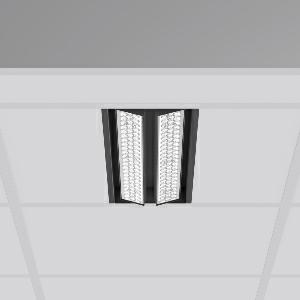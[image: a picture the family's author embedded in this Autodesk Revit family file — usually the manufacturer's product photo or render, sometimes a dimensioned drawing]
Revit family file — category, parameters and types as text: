
# Revit family: tx-move_901738_003_76_d800
name_source: partatom
category: Lighting Fixtures
units: mm (PartAtom-declared; Revit-internal decimal feet)

## family parameters
Cut with Voids When Loaded = No
Host = Face
Light Source = No
Part Type = Normal
Room Calculation Point = No
Round Connector Dimension = Use Diameter
Shared = No

## types (1)
- MultiLumen 1 (1 x LED Modul 830, 2625 lm, 3000)
    Apparent Load = 35 VA
    Approval mark = CE
    CIE Flux Codes = 65 90 98 100 100
    Color Rendering = 80
    Color Temperature = 3000
    Default Elevation = 1800 mm
    Description = Series: TX-MOVE
Einlege/Einbau-Flächenstrahler. Housing: sheet steel, powder-coated. 2xSwivel range: 90°. High-efficiency LED units with optimum light control thanks to clear plastic (PC) lens optics. Spezielle Mikrostrukturen reduzieren Gelbsaum. Asymmetrical light distribution. Suitable for laying in grid ceiling module 625. Connected converter included in separate gearbox.Suitable for through-wiring.MultiLumen: Luminous flux adjustable in 3 steps. Accessories: Mounting frame for installation in suspended ceilings. Environmentally friendly and resource-saving due to replaceable and recyclable components. 
Colour: deep black, matt (RAL 9005)
Length: 622 mm
Width: 190 mm
Height: 39 mm
Cut-out length: 602 mm
Cut-out width: 174 mm
Recess height: 100 mm
Lamp: LED
Socket: without socket
Colour temperature: 3000K
Colour rendering index (CRI): 80
System power: 35 W
Rated luminous flux: 5250 lm
Luminous efficiency: 150 lm/W
System power 2: 47 W
Rated luminous flux 2: 6800 lm
Luminous efficiency 2: 145 lm/W
System power 3: 68 W
Rated luminous flux 3: 9250 lm
Luminous efficiency 3: 136 lm/W
Control gear: Dimmable EVG, DALI
Protection class: I
Type of protection: IP 20
    Height = 0 mm  [stored 0 ft]
    Lamp = 1 x LED Modul 830
    Lamp Light Flux = 2625 lm
    Lamp count = 1
    Length = 622 mm
    Lifetime = 50000 h
    Luminous efficacy = 150 lm/W
    Manufacturer = RZB
    ModVariant = No
    Model = 901738.003.76
    Mounting Place = Ceiling, Wall
    Mounting Type = Recessed
    Number of Poles = 1
    OnlyDefault = Yes
    Power Factor = 1
    Product Name = TX-MOVE
    Product group = Recessed projectors
    ProductGroupID = 401
    Protection Class = Protection class I
    Protection Degree = IP 20
    RLX_Detail_Level = 1
    RLX_Emergency_Light_Flux = 0 lm
    RLX_Emergency_Type = 0
    RLX_Emergency_Type_DB = No
    RlxData = <blob elided: 56509 chars, md5=9f4b6286>
    Socket = socket
    Standby Power = 0 W
    System Light Flux = 5250 lm
    System Power = 35 W
    Type Comments = MultiLumen 1
    Type Image = 901737.003.jpg
    URL = http://relux.com
    VarID = multilumen_1
    Voltage = 230 V
    Voltage Range = 220-240 V
    Weight = 0.00 kg
    Width = 190 mm  [stored 0.62336 ft]

note: [stored X ft] marks values corroborated as IEEE doubles in the binary element streams (Revit-internal decimal feet)

## geometry (parser evidence)
native form markers: Blend x4, Sweep x16
no freeform markers — native parametric forms only
